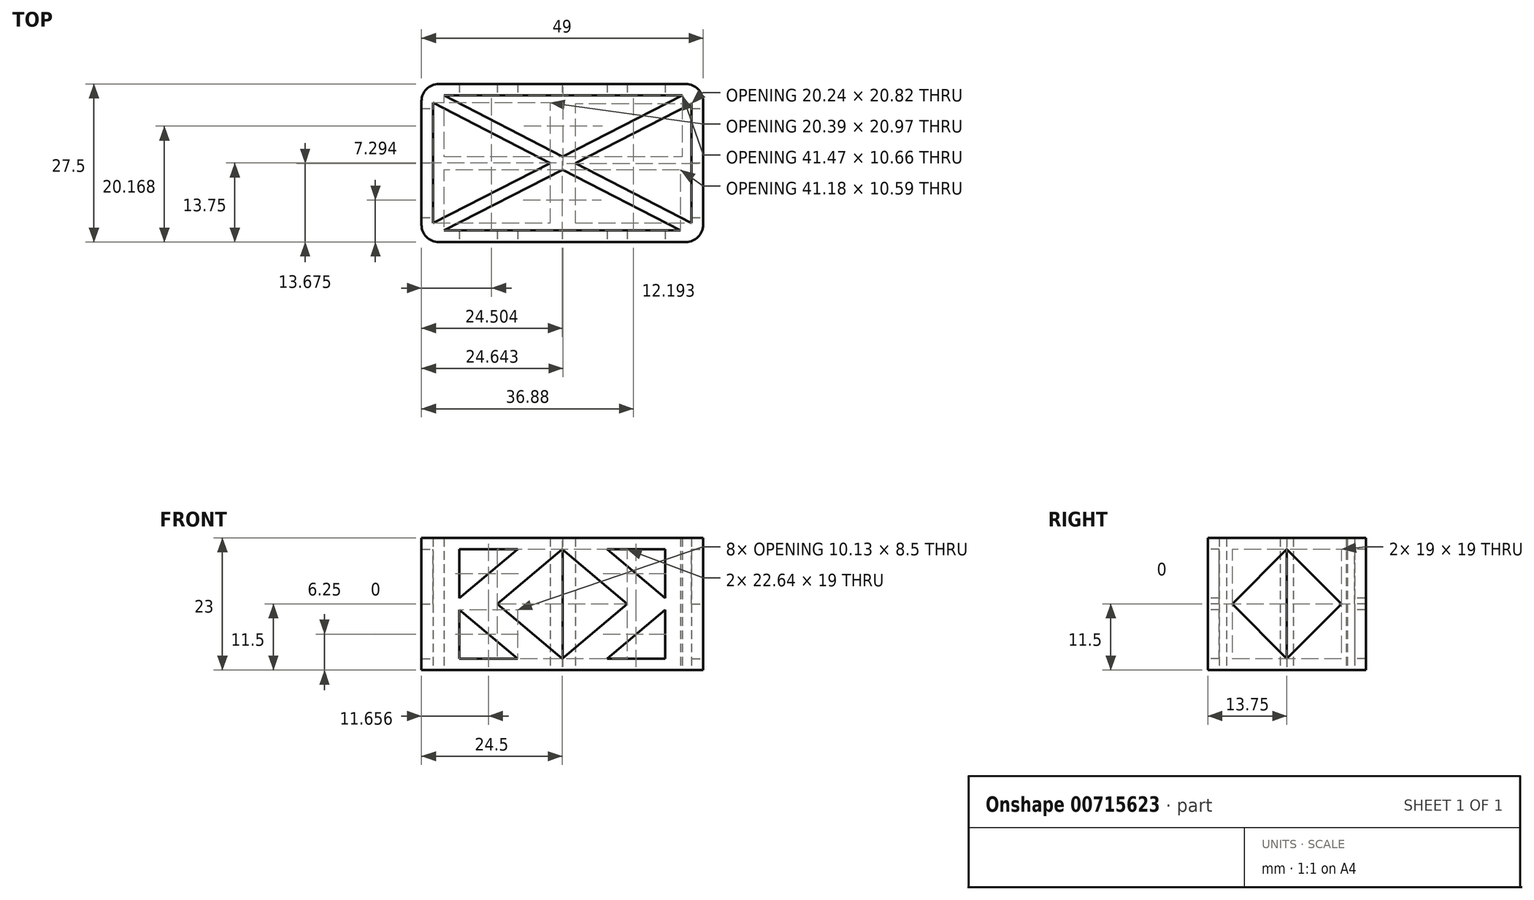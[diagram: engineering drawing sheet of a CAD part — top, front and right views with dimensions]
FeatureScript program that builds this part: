
annotation { "Feature Type Name" : "Feature", "Feature Type Description" : "" }
export const myFeature = defineFeature(function(context is Context, id is Id, definition is map)
    precondition{}
    {
        {
            var Q0;
            Q0=qCreatedBy(makeId("Top.planeOp"),FACE);
            var sketch = newSketch(context, id + "F0", { "sketchPlane" : qUnion([Q0])});
            skLineSegment(sketch, "E0.bottom", {"start": v(-21.5, -13.75) * mm, "end": v(21.5, -13.75) * mm});
            skLineSegment(sketch, "E0.top", {"start": v(-21.5, 13.75) * mm, "end": v(21.5, 13.75) * mm});
            skLineSegment(sketch, "E0.left", {"start": v(-24.5, -10.75) * mm, "end": v(-24.5, 10.75) * mm});
            skLineSegment(sketch, "E0.right", {"start": v(24.5, -10.75) * mm, "end": v(24.5, 10.75) * mm});
            skPoint(sketch, "E0.middle", {"position": v(0, 0) * mm});
            skPoint(sketch, "E1.visualSharp", {"position": v(-24.5, 13.75) * mm});
            skArc(sketch, "E1.filletArc", {"start": v(-21.5, 13.75) * mm, "mid": v(-23.62, 12.87) * mm, "end": v(-24.5, 10.75) * mm});
            skPoint(sketch, "E2.visualSharp", {"position": v(-24.5, -13.75) * mm});
            skArc(sketch, "E2.filletArc", {"start": v(-24.5, -10.75) * mm, "mid": v(-23.62, -12.87) * mm, "end": v(-21.5, -13.75) * mm});
            skPoint(sketch, "E3.visualSharp", {"position": v(24.5, -13.75) * mm});
            skArc(sketch, "E3.filletArc", {"start": v(21.5, -13.75) * mm, "mid": v(23.62, -12.87) * mm, "end": v(24.5, -10.75) * mm});
            skPoint(sketch, "E4.visualSharp", {"position": v(24.5, 13.75) * mm});
            skArc(sketch, "E4.filletArc", {"start": v(24.5, 10.75) * mm, "mid": v(23.62, 12.87) * mm, "end": v(21.5, 13.75) * mm});
            skArc(sketch, "E5.0", {"start": v(-22.5, -10.75) * mm, "mid": v(-22.2, -11.46) * mm, "end": v(-21.5, -11.75) * mm});
            skLineSegment(sketch, "E5.1", {"start": v(-21.5, -11.75) * mm, "end": v(21.5, -11.75) * mm});
            skLineSegment(sketch, "E5.2", {"start": v(-22.5, -10.75) * mm, "end": v(-22.5, 10.75) * mm});
            skArc(sketch, "E5.3", {"start": v(21.5, -11.75) * mm, "mid": v(22.2, -11.46) * mm, "end": v(22.5, -10.75) * mm});
            skArc(sketch, "E5.4", {"start": v(-21.5, 11.75) * mm, "mid": v(-22.2, 11.46) * mm, "end": v(-22.5, 10.75) * mm});
            skLineSegment(sketch, "E5.5", {"start": v(-21.5, 11.75) * mm, "end": v(21.5, 11.75) * mm});
            skArc(sketch, "E5.6", {"start": v(22.5, 10.75) * mm, "mid": v(22.2, 11.46) * mm, "end": v(21.5, 11.75) * mm});
            skLineSegment(sketch, "E5.7", {"start": v(22.5, -10.75) * mm, "end": v(22.5, 10.75) * mm});
            skLineSegment(sketch, "E6", {"start": v(-22.2, -11.46) * mm, "end": v(22.5, 11.46) * mm, "construction": true});
            skPoint(sketch, "E6.endSnap0", {"position": v(22.2, 11.46) * mm});
            skLineSegment(sketch, "E7", {"start": v(22.2, -11.46) * mm, "end": v(-22.2, 11.46) * mm, "construction": true});
            skLineSegment(sketch, "E8.0", {"start": v(22.5, -10.48) * mm, "end": v(2.26, -0.04) * mm});
            skLineSegment(sketch, "E9.0", {"start": v(20.6, -11.75) * mm, "end": v(0.07, -1.16) * mm});
            skLineSegment(sketch, "E10.0", {"start": v(-20.59, -11.75) * mm, "end": v(0.07, -1.16) * mm});
            skLineSegment(sketch, "E11.0", {"start": v(-22.5, -10.48) * mm, "end": v(-2.11, -0.03) * mm});
            skLineSegment(sketch, "E12.trimOffspring", {"start": v(2.26, -0.04) * mm, "end": v(22.5, 10.33) * mm});
            skLineSegment(sketch, "E13.trimOffspring", {"start": v(0.07, 1.09) * mm, "end": v(-20.6, 11.75) * mm});
            skLineSegment(sketch, "E14.trimOffspring", {"start": v(0.07, 1.09) * mm, "end": v(20.88, 11.75) * mm});
            skLineSegment(sketch, "E15.trimOffspring", {"start": v(-2.11, -0.03) * mm, "end": v(-22.5, 10.48) * mm});
            skSolve(sketch);
        }
        {
            var Q0;
            Q0=makeQuery(id+"F0.imprint","IMPRINT",FACE,{"disambiguationData":[TD([[makeQuery(id+"F0.imprint","IMPRINT",EDGE,{"derivedFrom":sQuery(id+"F0.wireOp",EDGE,"E0.bottom")}),1.0]])]});
            extrude(context, id + "F1", {"entities" : qUnion([Q0]), "depth" : 23 * mm, "offsetDistance" : 25 * mm});
        }
        {
            var Q0;
            Q0=makeQuery(id+"F1.opExtrude","SWEPT_FACE",FACE,{"disambiguationData":[OSD([sQuery(id+"F0.wireOp",EDGE,"E0.bottom")])]});
            var sketch = newSketch(context, id + "F2", { "sketchPlane" : qUnion([Q0])});
            skLineSegment(sketch, "E16", {"start": v(0, 23) * mm, "end": v(0, 0) * mm, "construction": true});
            skLineSegment(sketch, "E17", {"start": v(21.5, 11.5) * mm, "end": v(-21.5, 11.5) * mm, "construction": true});
            skLineSegment(sketch, "E18", {"start": v(0, 0) * mm, "end": v(0, 2) * mm, "construction": true});
            skLineSegment(sketch, "E19", {"start": v(0, 2) * mm, "end": v(-11.32, 11.5) * mm});
            skLineSegment(sketch, "E20", {"start": v(0, 23) * mm, "end": v(0, 21) * mm, "construction": true});
            skLineSegment(sketch, "E21", {"start": v(0, 21) * mm, "end": v(-11.32, 11.5) * mm});
            skLineSegment(sketch, "E22.MirrorCS", {"start": v(0, 2) * mm, "end": v(11.32, 11.5) * mm});
            skLineSegment(sketch, "E23.MirrorCS", {"start": v(0, 21) * mm, "end": v(11.32, 11.5) * mm});
            skLineSegment(sketch, "E24.0", {"start": v(-17.9, 21) * mm, "end": v(17.9, 21) * mm});
            skLineSegment(sketch, "E25.0", {"start": v(-17.9, 2) * mm, "end": v(17.9, 2) * mm});
            skLineSegment(sketch, "E26.0", {"start": v(-7.78, 21) * mm, "end": v(-17.9, 12.5) * mm});
            skLineSegment(sketch, "E26.1", {"start": v(7.78, 21) * mm, "end": v(17.9, 12.5) * mm});
            skLineSegment(sketch, "E26.2", {"start": v(7.78, 2) * mm, "end": v(17.9, 10.5) * mm});
            skLineSegment(sketch, "E26.3", {"start": v(-7.78, 2) * mm, "end": v(-17.9, 10.5) * mm});
            skLineSegment(sketch, "E27.0", {"start": v(-26.5, -5) * mm, "end": v(26.5, -5) * mm});
            skLineSegment(sketch, "E27.1", {"start": v(-26.5, 28) * mm, "end": v(-26.5, -5) * mm});
            skLineSegment(sketch, "E27.2", {"start": v(26.5, 28) * mm, "end": v(-26.5, 28) * mm});
            skLineSegment(sketch, "E27.3", {"start": v(26.5, -5) * mm, "end": v(26.5, 28) * mm});
            skLineSegment(sketch, "E28.0", {"start": v(21.5, 12.5) * mm, "end": v(-21.5, 12.5) * mm, "construction": true});
            skLineSegment(sketch, "E29.0", {"start": v(21.5, 10.5) * mm, "end": v(-21.5, 10.5) * mm, "construction": true});
            skLineSegment(sketch, "E30", {"start": v(-17.9, 10.5) * mm, "end": v(-17.9, 2) * mm});
            skLineSegment(sketch, "E31", {"start": v(-17.9, 12.5) * mm, "end": v(-17.9, 21) * mm});
            skLineSegment(sketch, "E32.MirrorCS", {"start": v(17.9, 10.5) * mm, "end": v(17.9, 2) * mm});
            skLineSegment(sketch, "E33.MirrorCS", {"start": v(17.9, 12.5) * mm, "end": v(17.9, 21) * mm});
            skSolve(sketch);
        }
        {
            var Q0;
            {var subQ2=sQuery(id+"F2.wireOp",EDGE,"E26.0");Q0=makeQuery(id+"F2.imprint","IMPRINT",FACE,{"disambiguationData":[TD([[makeQuery(id+"F2.imprint","IMPRINT",EDGE,{"derivedFrom":subQ2}),-1.0]])]});}
            var Q1;
            Q1=makeQuery(id+"F2.imprint","IMPRINT",FACE,{"disambiguationData":[TD([[makeQuery(id+"F2.imprint","IMPRINT",EDGE,{"derivedFrom":sQuery(id+"F2.wireOp",EDGE,"E19")}),-1.0]])]});
            var Q2;
            {var subQ2=sQuery(id+"F2.wireOp",EDGE,"E26.3");Q2=makeQuery(id+"F2.imprint","IMPRINT",FACE,{"disambiguationData":[TD([[makeQuery(id+"F2.imprint","IMPRINT",EDGE,{"derivedFrom":subQ2}),1.0]])]});}
            var Q3;
            {var subQ2=sQuery(id+"F2.wireOp",EDGE,"E26.2");Q3=makeQuery(id+"F2.imprint","IMPRINT",FACE,{"disambiguationData":[TD([[makeQuery(id+"F2.imprint","IMPRINT",EDGE,{"derivedFrom":subQ2}),-1.0]])]});}
            var Q4;
            {var subQ2=sQuery(id+"F2.wireOp",EDGE,"E26.1");Q4=makeQuery(id+"F2.imprint","IMPRINT",FACE,{"disambiguationData":[TD([[makeQuery(id+"F2.imprint","IMPRINT",EDGE,{"derivedFrom":subQ2}),1.0]])]});}
            extrude(context, id + "F3", {"entities" : qUnion([Q0, Q1, Q2, Q3, Q4]), "operationType" : NewBodyOperationType.REMOVE, "oppositeDirection" : true, "depth" : 40 * mm, "offsetDistance" : 25 * mm});
        }
        {
            var Q0;
            Q0=makeQuery(id+"F1.opExtrude","SWEPT_FACE",FACE,{"disambiguationData":[OSD([sQuery(id+"F0.wireOp",EDGE,"E0.right")])]});
            var sketch = newSketch(context, id + "F4", { "sketchPlane" : qUnion([Q0])});
            skLineSegment(sketch, "E34", {"start": v(0, 0) * mm, "end": v(0, 23) * mm, "construction": true});
            skLineSegment(sketch, "E35", {"start": v(-10.75, 11.5) * mm, "end": v(10.75, 11.5) * mm, "construction": true});
            skLineSegment(sketch, "E36", {"start": v(0, 0) * mm, "end": v(0, 2) * mm, "construction": true});
            skLineSegment(sketch, "E37", {"start": v(0, 2) * mm, "end": v(-9.5, 11.5) * mm});
            skLineSegment(sketch, "E38.MirrorCS", {"start": v(0, 21) * mm, "end": v(-9.5, 11.5) * mm});
            skLineSegment(sketch, "E39.MirrorCS", {"start": v(0, 2) * mm, "end": v(9.5, 11.5) * mm});
            skLineSegment(sketch, "E40.MirrorCS", {"start": v(0, 21) * mm, "end": v(9.5, 11.5) * mm});
            skSolve(sketch);
        }
        {
            var Q0;
            Q0=makeQuery(id+"F4.imprint","IMPRINT",FACE,{"disambiguationData":[TD([[makeQuery(id+"F4.imprint","IMPRINT",EDGE,{"derivedFrom":sQuery(id+"F4.wireOp",EDGE,"E37")}),-1.0]])]});
            extrude(context, id + "F5", {"entities" : qUnion([Q0]), "operationType" : NewBodyOperationType.REMOVE, "oppositeDirection" : true, "depth" : 60 * mm, "offsetDistance" : 25 * mm});
        }
        {
            var Q0;
            {var subQ8=sQuery(id+"F0.wireOp",EDGE,"E5.0");Q0=makeQuery(id+"F0.imprint","IMPRINT",FACE,{"disambiguationData":[TD([[makeQuery(id+"F0.imprint","IMPRINT",EDGE,{"derivedFrom":subQ8}),1.0]])]});}
            extrude(context, id + "F6", {"entities" : qUnion([Q0]), "operationType" : NewBodyOperationType.ADD, "depth" : 23 * mm, "offsetDistance" : 25 * mm});
        }
    });
